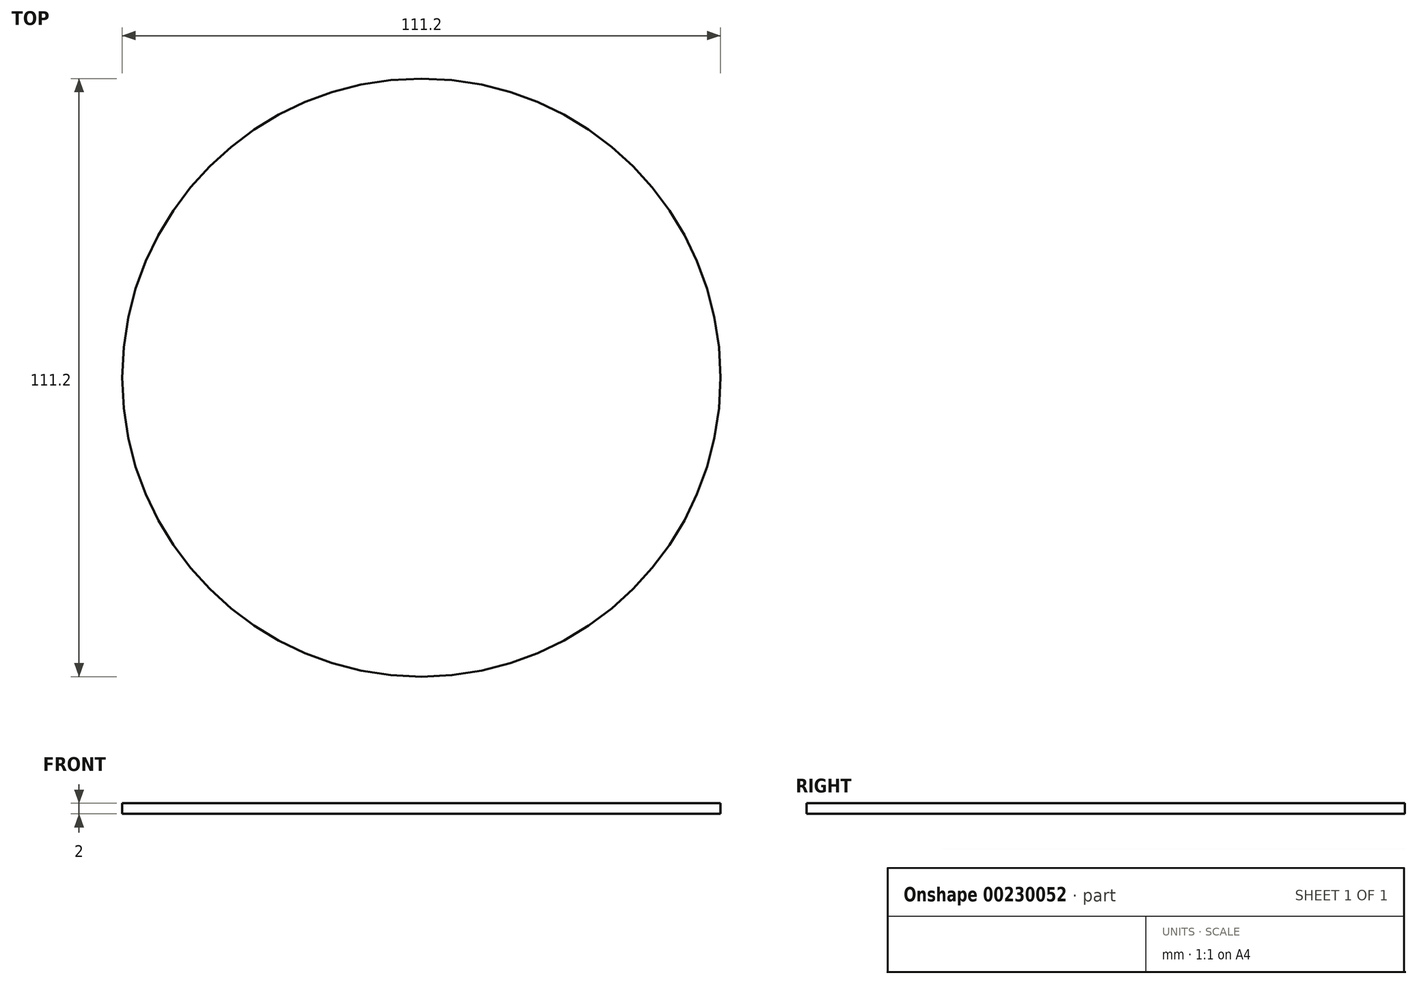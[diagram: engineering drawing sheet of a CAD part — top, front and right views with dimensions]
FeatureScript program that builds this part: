
annotation { "Feature Type Name" : "Feature", "Feature Type Description" : "" }
export const myFeature = defineFeature(function(context is Context, id is Id, definition is map)
    precondition{}
    {
        {
            var Q0;
            Q0=qCreatedBy(makeId("Top.planeOp"),FACE);
            var sketch = newSketch(context, id + "F0", { "sketchPlane" : qUnion([Q0])});
            skCircle(sketch, "E0", {"center": v(0, 0) * mm, "radius": 55.6 * mm});
            skSolve(sketch);
        }
        {
            var Q0;
            Q0=makeQuery(id+"F0.imprint","IMPRINT",FACE,{"disambiguationData":[TD([[makeQuery(id+"F0.imprint","IMPRINT",EDGE,{"derivedFrom":sQuery(id+"F0.wireOp",EDGE,"E0")}),1.0]])]});
            extrude(context, id + "F1", {"entities" : qUnion([Q0]), "depth" : 2 * mm});
        }
    });
